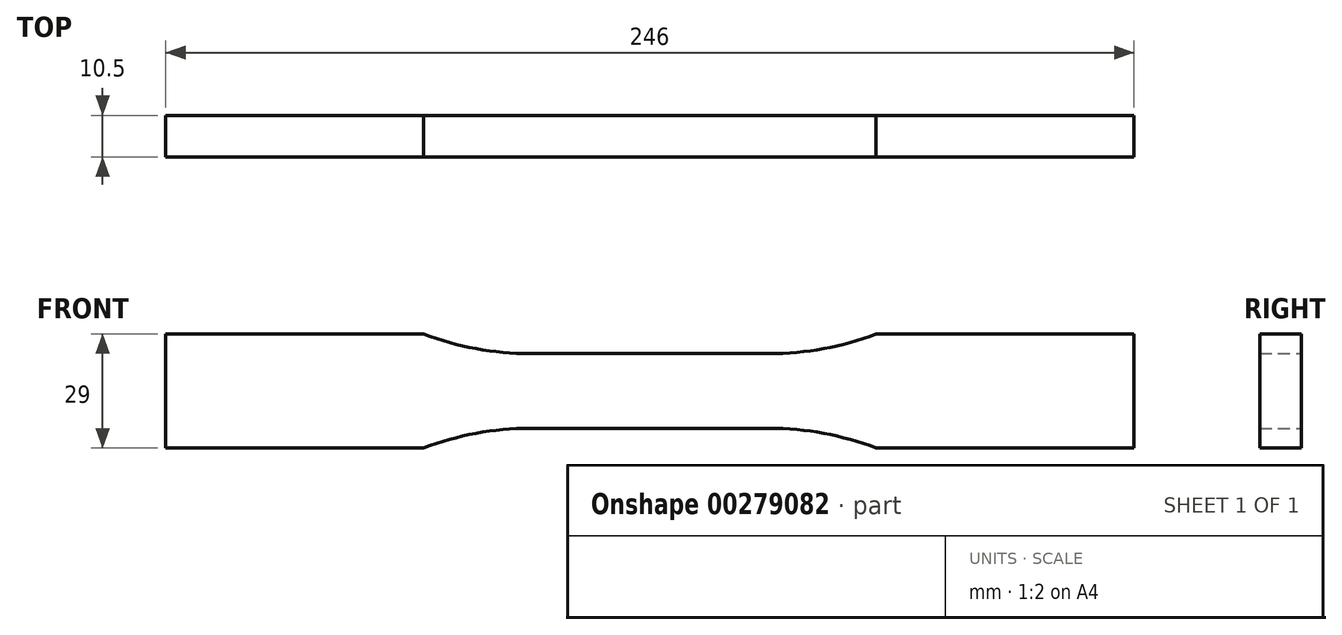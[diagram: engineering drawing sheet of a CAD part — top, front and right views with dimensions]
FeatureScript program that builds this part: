
annotation { "Feature Type Name" : "Feature", "Feature Type Description" : "" }
export const myFeature = defineFeature(function(context is Context, id is Id, definition is map)
    precondition{}
    {
        {
            var Q0;
            Q0=qCreatedBy(makeId("Front.planeOp"),FACE);
            var sketch = newSketch(context, id + "F0", { "sketchPlane" : qUnion([Q0])});
            skLineSegment(sketch, "E0", {"start": v(0, 9.5) * mm, "end": v(30.39, 9.5) * mm});
            skArc(sketch, "E1", {"start": v(30.39, 9.5) * mm, "mid": v(44.17, 10.76) * mm, "end": v(57.5, 14.5) * mm});
            skLineSegment(sketch, "E2", {"start": v(57.5, 14.5) * mm, "end": v(123, 14.5) * mm});
            skLineSegment(sketch, "E3.MirrorCS", {"start": v(-57.5, 14.5) * mm, "end": v(-123, 14.5) * mm});
            skLineSegment(sketch, "E4.MirrorCS", {"start": v(0, 9.5) * mm, "end": v(-30.39, 9.5) * mm});
            skArc(sketch, "E5.MirrorCS", {"start": v(-30.39, 9.5) * mm, "mid": v(-44.17, 10.76) * mm, "end": v(-57.5, 14.5) * mm});
            skLineSegment(sketch, "E6.MirrorCS", {"start": v(0, -9.5) * mm, "end": v(30.39, -9.5) * mm});
            skArc(sketch, "E7.MirrorCS", {"start": v(30.39, -9.5) * mm, "mid": v(44.17, -10.76) * mm, "end": v(57.5, -14.5) * mm});
            skLineSegment(sketch, "E8.MirrorCS", {"start": v(57.5, -14.5) * mm, "end": v(123, -14.5) * mm});
            skLineSegment(sketch, "E9.MirrorCS", {"start": v(-57.5, -14.5) * mm, "end": v(-123, -14.5) * mm});
            skArc(sketch, "E10.MirrorCS", {"start": v(-30.39, -9.5) * mm, "mid": v(-44.17, -10.76) * mm, "end": v(-57.5, -14.5) * mm});
            skLineSegment(sketch, "E11.MirrorCS", {"start": v(0, -9.5) * mm, "end": v(-30.39, -9.5) * mm});
            skLineSegment(sketch, "E12", {"start": v(-123, 14.5) * mm, "end": v(-123, -14.5) * mm});
            skLineSegment(sketch, "E13", {"start": v(123, 14.5) * mm, "end": v(123, -14.5) * mm});
            skSolve(sketch);
        }
        {
            var Q0;
            Q0=makeQuery(id+"F0.imprint","IMPRINT",FACE,{"disambiguationData":[TD([[makeQuery(id+"F0.imprint","IMPRINT",EDGE,{"derivedFrom":sQuery(id+"F0.wireOp",EDGE,"E1")}),-1.0]])]});
            extrude(context, id + "F1", {"entities" : qUnion([Q0]), "endBound" : BoundingType.SYMMETRIC, "depth" : 10.5 * mm});
        }
    });
